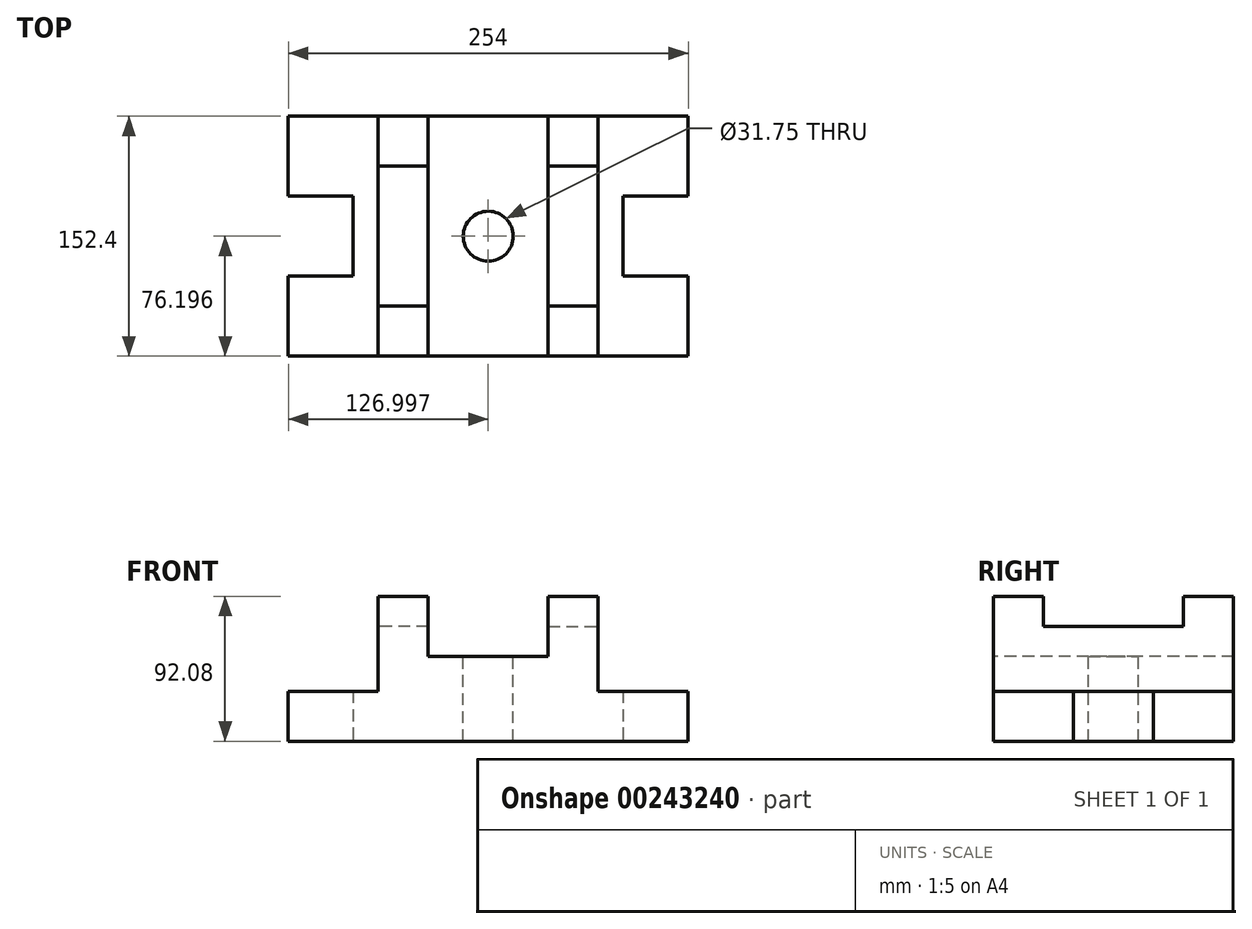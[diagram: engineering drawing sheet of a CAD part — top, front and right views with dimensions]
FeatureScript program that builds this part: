
annotation { "Feature Type Name" : "Feature", "Feature Type Description" : "" }
export const myFeature = defineFeature(function(context is Context, id is Id, definition is map)
    precondition{}
    {
        {
            var Q0;
            Q0=qCreatedBy(makeId("Top.planeOp"),FACE);
            var sketch = newSketch(context, id + "F0", { "sketchPlane" : qUnion([Q0])});
            skLineSegment(sketch, "E0.bottom", {"start": v(-134.9, 5.06) * mm, "end": v(119.1, 5.06) * mm});
            skLineSegment(sketch, "E0.top", {"start": v(-134.9, -45.74) * mm, "end": v(119.1, -45.74) * mm});
            skLineSegment(sketch, "E0.left", {"start": v(-134.9, 5.06) * mm, "end": v(-134.9, -45.74) * mm});
            skLineSegment(sketch, "E0.right", {"start": v(119.1, 5.06) * mm, "end": v(119.1, -45.74) * mm});
            skLineSegment(sketch, "E1.bottom", {"start": v(-93.62, 55.86) * mm, "end": v(77.83, 55.86) * mm});
            skLineSegment(sketch, "E1.top", {"start": v(-93.62, 5.06) * mm, "end": v(77.83, 5.06) * mm});
            skLineSegment(sketch, "E1.left", {"start": v(-93.62, 55.86) * mm, "end": v(-93.62, 5.06) * mm});
            skLineSegment(sketch, "E1.right", {"start": v(77.83, 55.86) * mm, "end": v(77.83, 5.06) * mm});
            skLineSegment(sketch, "E2.bottom", {"start": v(-134.9, 106.66) * mm, "end": v(119.1, 106.66) * mm});
            skLineSegment(sketch, "E2.top", {"start": v(-134.9, 55.86) * mm, "end": v(119.1, 55.86) * mm});
            skLineSegment(sketch, "E2.left", {"start": v(-134.9, 106.66) * mm, "end": v(-134.9, 55.86) * mm});
            skLineSegment(sketch, "E2.right", {"start": v(119.1, 106.66) * mm, "end": v(119.1, 55.86) * mm});
            skSolve(sketch);
        }
        {
            var Q0;
            Q0 = qSketchRegion(id + "F0", true);
            extrude(context, id + "F1", {"entities" : qUnion([Q0]), "depth" : 31.75 * mm});
        }
        {
            var Q0;
            Q0=makeQuery(id+"F1.opExtrude","CAP_FACE",FACE,{"disambiguationData":[OSD([sQuery(id+"F0.wireOp",EDGE,"E0.bottom"),sQuery(id+"F0.wireOp",EDGE,"E0.top"),sQuery(id+"F0.wireOp",EDGE,"E0.left"),sQuery(id+"F0.wireOp",EDGE,"E0.right"),sQuery(id+"F0.wireOp",EDGE,"E1.left"),sQuery(id+"F0.wireOp",EDGE,"E1.right"),sQuery(id+"F0.wireOp",EDGE,"E2.bottom"),sQuery(id+"F0.wireOp",EDGE,"E2.top"),sQuery(id+"F0.wireOp",EDGE,"E2.left"),sQuery(id+"F0.wireOp",EDGE,"E2.right")])],"isStart":false});
            var sketch = newSketch(context, id + "F2", { "sketchPlane" : qUnion([Q0])});
            skLineSegment(sketch, "E3.bottom", {"start": v(-46, 106.66) * mm, "end": v(30.2, 106.66) * mm});
            skLineSegment(sketch, "E3.top", {"start": v(-46, -45.74) * mm, "end": v(30.2, -45.74) * mm});
            skLineSegment(sketch, "E3.left", {"start": v(-46, 106.66) * mm, "end": v(-46, -45.74) * mm});
            skLineSegment(sketch, "E3.right", {"start": v(30.2, 106.66) * mm, "end": v(30.2, -45.74) * mm});
            skSolve(sketch);
        }
        {
            var Q0;
            Q0 = qSketchRegion(id + "F2", true);
            extrude(context, id + "F3", {"entities" : qUnion([Q0]), "operationType" : NewBodyOperationType.ADD, "depth" : 22.22 * mm});
        }
        {
            var Q0;
            Q0=makeQuery(id+"F3.opExtrude","CAP_FACE",FACE,{"disambiguationData":[OSD([sQuery(id+"F2.wireOp",EDGE,"E3.bottom"),sQuery(id+"F2.wireOp",EDGE,"E3.top"),sQuery(id+"F2.wireOp",EDGE,"E3.left"),sQuery(id+"F2.wireOp",EDGE,"E3.right")])],"isStart":false});
            var sketch = newSketch(context, id + "F4", { "sketchPlane" : qUnion([Q0])});
            skCircle(sketch, "E4", {"center": v(-7.9, 30.46) * mm, "radius": 15.88 * mm});
            skSolve(sketch);
        }
        {
            var Q0;
            Q0=makeQuery(id+"F4.imprint","IMPRINT",FACE,{"disambiguationData":[TD([[makeQuery(id+"F4.imprint","IMPRINT",EDGE,{"derivedFrom":sQuery(id+"F4.wireOp",EDGE,"E4")}),1.0]])]});
            extrude(context, id + "F5", {"entities" : qUnion([Q0]), "operationType" : NewBodyOperationType.REMOVE, "endBound" : BoundingType.THROUGH_ALL, "oppositeDirection" : true, "depth" : 25.4 * mm});
        }
        {
            var Q0;
            {var subQ0=sQuery(id+"F0.wireOp",EDGE,"E0.right");var subQ1=sQuery(id+"F0.wireOp",EDGE,"E0.top");var subQ2=sQuery(id+"F0.wireOp",EDGE,"E1.right");var subQ3=sQuery(id+"F0.wireOp",EDGE,"E0.bottom");var subQ4=sQuery(id+"F0.wireOp",EDGE,"E2.bottom");var subQ5=sQuery(id+"F0.wireOp",EDGE,"E2.top");var subQ6=sQuery(id+"F0.wireOp",EDGE,"E2.right");Q0=makeQuery(id+"F3.boolean.opBoolean","SPLIT",FACE,{"disambiguationData":[TD([makeQuery(id+"F1.opExtrude","SWEPT_FACE",FACE,{"disambiguationData":[OSD([subQ0])]})])],"derivedFrom":makeQuery(id+"F1.opExtrude","CAP_FACE",FACE,{"disambiguationData":[OSD([subQ3,subQ1,sQuery(id+"F0.wireOp",EDGE,"E0.left"),subQ0,sQuery(id+"F0.wireOp",EDGE,"E1.left"),subQ2,subQ4,subQ5,sQuery(id+"F0.wireOp",EDGE,"E2.left"),subQ6])],"isStart":false})});}
            var sketch = newSketch(context, id + "F6", { "sketchPlane" : qUnion([Q0])});
            skLineSegment(sketch, "E5.bottom", {"start": v(-46, 106.66) * mm, "end": v(-77.74, 106.66) * mm});
            skLineSegment(sketch, "E5.top", {"start": v(-46, -45.74) * mm, "end": v(-77.74, -45.74) * mm});
            skLineSegment(sketch, "E5.left", {"start": v(-46, 106.66) * mm, "end": v(-46, -45.74) * mm});
            skLineSegment(sketch, "E5.right", {"start": v(-77.74, 106.66) * mm, "end": v(-77.74, -45.74) * mm});
            skLineSegment(sketch, "E6.bottom", {"start": v(30.2, 106.66) * mm, "end": v(61.96, 106.66) * mm});
            skLineSegment(sketch, "E6.top", {"start": v(30.2, -45.74) * mm, "end": v(61.96, -45.74) * mm});
            skLineSegment(sketch, "E6.left", {"start": v(30.2, 106.66) * mm, "end": v(30.2, -45.74) * mm});
            skLineSegment(sketch, "E6.right", {"start": v(61.96, 106.66) * mm, "end": v(61.96, -45.74) * mm});
            skSolve(sketch);
        }
        {
            var Q0;
            Q0 = qSketchRegion(id + "F6", true);
            extrude(context, id + "F7", {"entities" : qUnion([Q0]), "operationType" : NewBodyOperationType.ADD, "depth" : 60.32 * mm});
        }
        {
            var Q0;
            Q0=makeQuery(id+"F7.opExtrude","CAP_FACE",FACE,{"disambiguationData":[OSD([sQuery(id+"F6.wireOp",EDGE,"E6.bottom"),sQuery(id+"F6.wireOp",EDGE,"E6.top"),sQuery(id+"F6.wireOp",EDGE,"E6.left"),sQuery(id+"F6.wireOp",EDGE,"E6.right")])],"isStart":false});
            var sketch = newSketch(context, id + "F8", { "sketchPlane" : qUnion([Q0])});
            skLineSegment(sketch, "E7.bottom", {"start": v(-46, 74.9) * mm, "end": v(-77.74, 74.9) * mm});
            skLineSegment(sketch, "E7.top", {"start": v(-46, -14) * mm, "end": v(-77.74, -14) * mm});
            skLineSegment(sketch, "E7.left", {"start": v(-46, 74.9) * mm, "end": v(-46, -14) * mm});
            skLineSegment(sketch, "E7.right", {"start": v(-77.74, 74.9) * mm, "end": v(-77.74, -14) * mm});
            skLineSegment(sketch, "E8.bottom", {"start": v(30.2, 74.9) * mm, "end": v(61.96, 74.9) * mm});
            skLineSegment(sketch, "E8.top", {"start": v(30.2, -14) * mm, "end": v(61.96, -14) * mm});
            skLineSegment(sketch, "E8.left", {"start": v(30.2, 74.9) * mm, "end": v(30.2, -14) * mm});
            skLineSegment(sketch, "E8.right", {"start": v(61.96, 74.9) * mm, "end": v(61.96, -14) * mm});
            skSolve(sketch);
        }
        {
            var Q0;
            Q0 = qSketchRegion(id + "F8", true);
            extrude(context, id + "F9", {"entities" : qUnion([Q0]), "operationType" : NewBodyOperationType.REMOVE, "oppositeDirection" : true, "depth" : 19.05 * mm});
        }
    });
